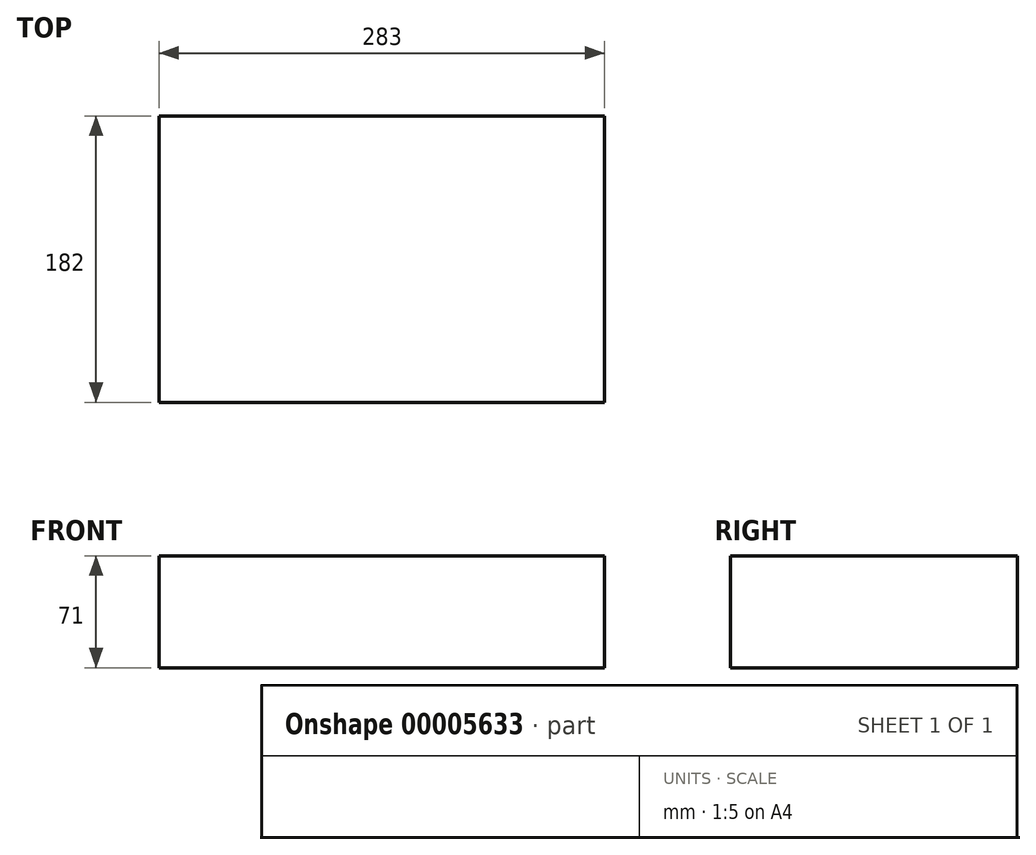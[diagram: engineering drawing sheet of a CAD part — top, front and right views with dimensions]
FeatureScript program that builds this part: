
annotation { "Feature Type Name" : "Feature", "Feature Type Description" : "" }
export const myFeature = defineFeature(function(context is Context, id is Id, definition is map)
    precondition{}
    {
        {
            var Q0;
            Q0=qCreatedBy(makeId("Top.planeOp"),FACE);
            var sketch = newSketch(context, id + "F0", { "sketchPlane" : qUnion([Q0])});
            skLineSegment(sketch, "E0.bottom", {"start": v(0, 0) * mm, "end": v(283, 0) * mm});
            skLineSegment(sketch, "E0.top", {"start": v(0, 182) * mm, "end": v(283, 182) * mm});
            skLineSegment(sketch, "E0.left", {"start": v(0, 0) * mm, "end": v(0, 182) * mm});
            skLineSegment(sketch, "E0.right", {"start": v(283, 0) * mm, "end": v(283, 182) * mm});
            skSolve(sketch);
        }
        {
            var Q0;
            Q0=makeQuery(id+"F0.imprint","IMPRINT",FACE,{"disambiguationData":[TD([[makeQuery(id+"F0.imprint","IMPRINT",EDGE,{"derivedFrom":sQuery(id+"F0.wireOp",EDGE,"E0.bottom")}),1.0]])]});
            extrude(context, id + "F1", {"entities" : qUnion([Q0]), "depth" : 71 * mm});
        }
    });
